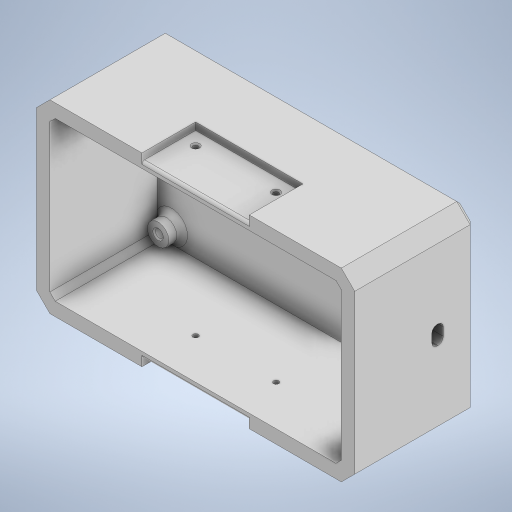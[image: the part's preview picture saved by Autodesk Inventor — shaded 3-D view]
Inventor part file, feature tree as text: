
AUTODESK INVENTOR PART (.ipt)
format: ipt  version: 2023 (Build 270158000, 158)  size: 364,032 bytes
history: native  units: mm
features: extrude x7, sketch x5, fillet x4, chamfer x4, projected_geometry x3, other x2, hole x1
ambient origin geometry x8: Origin, YZ Plane, XZ Plane, XY Plane, X Axis, Y Axis, Z Axis, Center Point
bodies: Body1 (feature_tree)
feature tree (26):
  other  "솔리드1"
  sketch  "스케치1"
  extrude  "돌출1"  Depth=108.6mm
  extrude  "돌출2"  Depth=59.0mm
  extrude  "돌출4"  Depth=8.0mm
  hole  "구멍1"  [1 undecoded]
  fillet  "모깎기2"  Radius=47.5mm
  other  "작업 평면1"
  sketch  "스케치3"
  extrude  "돌출5"  Depth=98.0mm
  extrude  "돌출6"  Depth=5.0mm TaperAngle=0.0deg
  fillet  "모깎기4"  Radius=40.0mm
  fillet  "모깎기6"  Radius=5.0mm
  extrude  "돌출7"  Depth=2.0mm
  extrude  "돌출8"  Depth=7.0mm
  chamfer  "모따기1"  Distance=3.0mm
  chamfer  "모따기2"  Distance=7.0mm
  chamfer  "모따기3"  Distance=4.3mm
  fillet  "모깎기7"  Radius=2.0mm
  chamfer  "모따기4"  Distance=2.0mm
  sketch  "스케치2"
  projected_geometry  "투영된 루프1"
  projected_geometry  "투영된 루프2"
  projected_geometry  "투영된 루프3"
  sketch  "스케치4"
  sketch  "스케치5"
note: 1 required parameter value undecoded (feature->parameter linkage not recoverable at this tier; creation-order binding heuristic only, values carry confidence <= 0.55)
